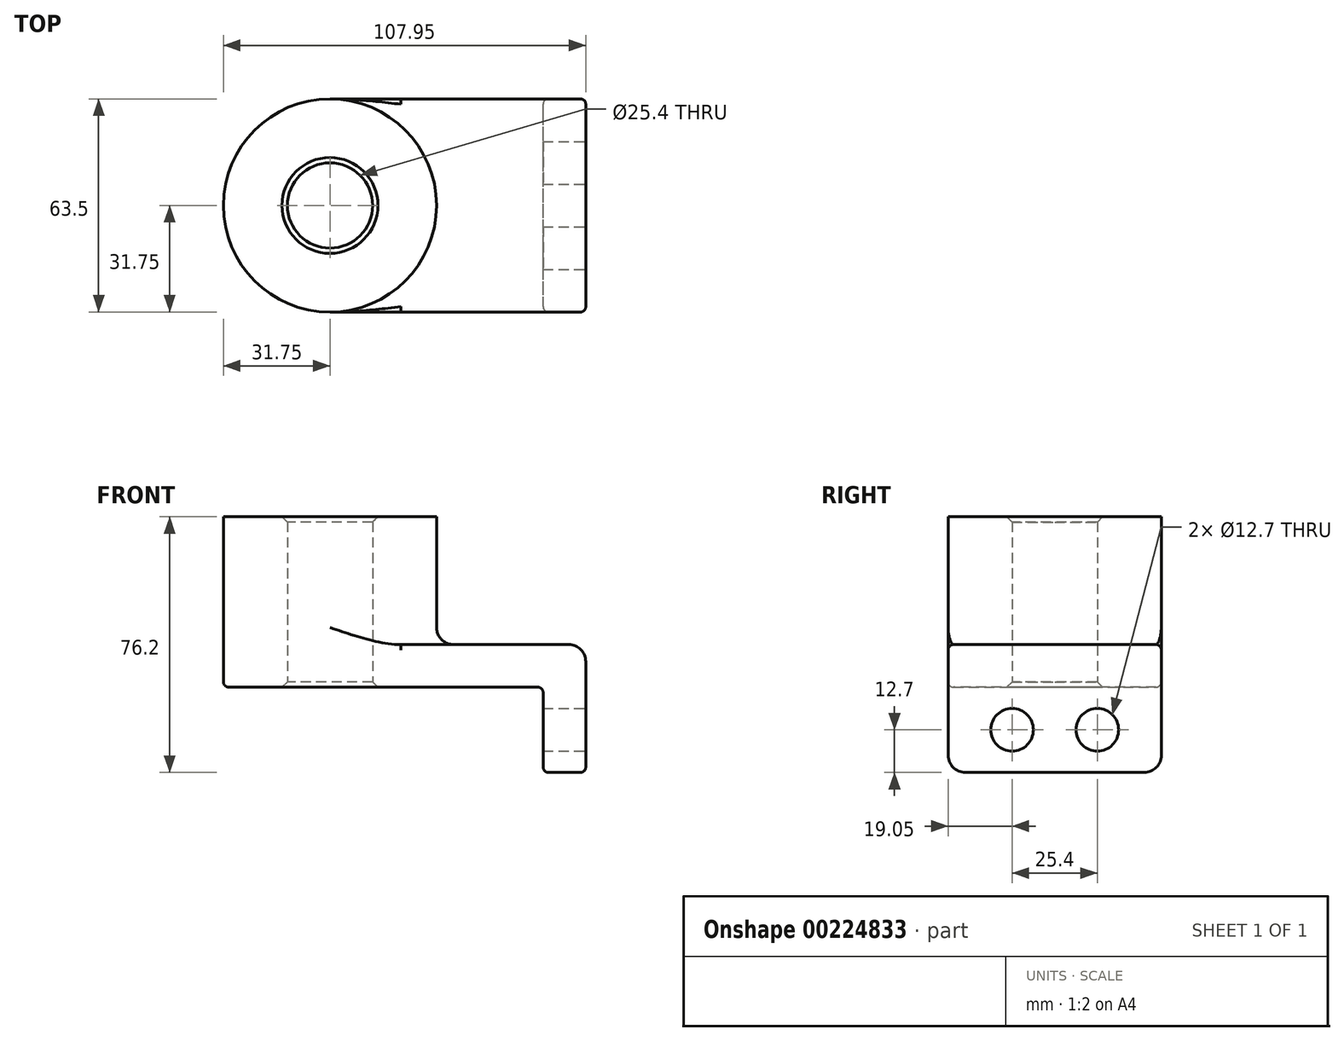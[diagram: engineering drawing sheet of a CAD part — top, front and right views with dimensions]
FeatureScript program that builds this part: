
annotation { "Feature Type Name" : "Feature", "Feature Type Description" : "" }
export const myFeature = defineFeature(function(context is Context, id is Id, definition is map)
    precondition{}
    {
        {
            var Q0;
            Q0=qCreatedBy(makeId("Top.planeOp"),FACE);
            var sketch = newSketch(context, id + "F0", { "sketchPlane" : qUnion([Q0])});
            skLineSegment(sketch, "E0.bottom", {"start": v(-38.1, 31.75) * mm, "end": v(38.1, 31.75) * mm});
            skLineSegment(sketch, "E0.top", {"start": v(-38.1, -31.75) * mm, "end": v(38.1, -31.75) * mm});
            skLineSegment(sketch, "E0.left", {"start": v(-38.1, 31.75) * mm, "end": v(-38.1, -31.75) * mm});
            skLineSegment(sketch, "E0.right", {"start": v(38.1, 31.75) * mm, "end": v(38.1, -31.75) * mm});
            skPoint(sketch, "E0.middle", {"position": v(0, 0) * mm});
            skCircle(sketch, "E1", {"center": v(-38.1, 0) * mm, "radius": 31.75 * mm});
            skCircle(sketch, "E2", {"center": v(-38.1, 0) * mm, "radius": 12.7 * mm});
            skSolve(sketch);
        }
        {
            var Q0;
            Q0 = qSketchRegion(id + "F0", true);
            extrude(context, id + "F1", {"entities" : qUnion([Q0]), "depth" : 12.7 * mm});
        }
        {
            var Q0;
            {var subQ1=sQuery(id+"F0.wireOp",EDGE,"E0.left");var subQ3=sQuery(id+"F0.wireOp",EDGE,"E2");var subQ4=makeQuery(id+"F0.imprint","INTERSECT",VERTEX,{"disambiguationData":[OD(0.0)],"derivedFrom":[subQ1,subQ3]});Q0=makeQuery(id+"F0.imprint","IMPRINT",FACE,{"disambiguationData":[TD([[makeQuery(id+"F0.imprint","IMPRINT",EDGE,{"disambiguationData":[TD([[subQ4,-1.0]])],"derivedFrom":subQ3}),-1.0]])]});}
            var Q1;
            {var subQ1=sQuery(id+"F0.wireOp",EDGE,"E0.left");var subQ3=sQuery(id+"F0.wireOp",EDGE,"E2");var subQ4=makeQuery(id+"F0.imprint","INTERSECT",VERTEX,{"disambiguationData":[OD(0.0)],"derivedFrom":[subQ1,subQ3]});Q1=makeQuery(id+"F0.imprint","IMPRINT",FACE,{"disambiguationData":[TD([[makeQuery(id+"F0.imprint","IMPRINT",EDGE,{"disambiguationData":[TD([[subQ4,1.0]])],"derivedFrom":subQ3}),-1.0]])]});}
            extrude(context, id + "F2", {"entities" : qUnion([Q0, Q1]), "operationType" : NewBodyOperationType.ADD, "depth" : 50.8 * mm});
        }
        {
            var Q0;
            Q0=makeQuery(id+"F1.opExtrude","SWEPT_FACE",FACE,{"disambiguationData":[OSD([sQuery(id+"F0.wireOp",EDGE,"E0.right")])]});
            var sketch = newSketch(context, id + "F3", { "sketchPlane" : qUnion([Q0])});
            skLineSegment(sketch, "E3.bottom", {"start": v(-31.75, 12.7) * mm, "end": v(31.75, 12.7) * mm});
            skLineSegment(sketch, "E3.top", {"start": v(-31.75, -25.4) * mm, "end": v(31.75, -25.4) * mm});
            skLineSegment(sketch, "E3.left", {"start": v(-31.75, 12.7) * mm, "end": v(-31.75, -25.4) * mm});
            skLineSegment(sketch, "E3.right", {"start": v(31.75, 12.7) * mm, "end": v(31.75, -25.4) * mm});
            skCircle(sketch, "E4", {"center": v(-12.7, -12.7) * mm, "radius": 6.35 * mm});
            skLineSegment(sketch, "E5", {"start": v(0, 0) * mm, "end": v(0, -25.4) * mm});
            skCircle(sketch, "E6.MirrorC", {"center": v(12.7, -12.7) * mm, "radius": 6.35 * mm});
            skSolve(sketch);
        }
        {
            var Q0;
            Q0 = qSketchRegion(id + "F3", true);
            extrude(context, id + "F4", {"entities" : qUnion([Q0]), "operationType" : NewBodyOperationType.ADD, "oppositeDirection" : true, "depth" : 12.7 * mm});
        }
        {
            var Q0;
            {var subQ0=sQuery(id+"F0.wireOp",EDGE,"E1");Q0=makeQuery(id+"F2.boolean.opBoolean","INTERSECT",EDGE,{"derivedFrom":[makeQuery(id+"F1.opExtrude","CAP_FACE",FACE,{"disambiguationData":[OSD([sQuery(id+"F0.wireOp",EDGE,"E0.bottom"),sQuery(id+"F0.wireOp",EDGE,"E0.top"),sQuery(id+"F0.wireOp",EDGE,"E0.right"),subQ0,sQuery(id+"F0.wireOp",EDGE,"E2")])],"isStart":false}),makeQuery(id+"F2.opExtrude","SWEPT_FACE",FACE,{"disambiguationData":[OSD([subQ0])]})]});}
            var Q1;
            Q1=makeQuery(id+"F1.opExtrude","CAP_EDGE",EDGE,{"disambiguationData":[OSD([sQuery(id+"F0.wireOp",EDGE,"E0.right")])],"isStart":false});
            var Q2;
            Q2=makeQuery(id+"F4.opExtrude","SWEPT_EDGE",EDGE,{"disambiguationData":[OSD([sQuery(id+"F3.wireOp",EDGE,"E3.top"),sQuery(id+"F3.wireOp",EDGE,"E3.left")])]});
            var Q3;
            Q3=makeQuery(id+"F4.opExtrude","SWEPT_EDGE",EDGE,{"disambiguationData":[OSD([sQuery(id+"F3.wireOp",EDGE,"E3.top"),sQuery(id+"F3.wireOp",EDGE,"E3.right")])]});
            fillet(context, id + "F5", {"entities" : qUnion([Q0, Q1, Q2, Q3]), "radius" : 5.08 * mm, "tangentPropagation" : true, "allowEdgeOverflow" : false});
        }
        {
            var Q0;
            Q0=makeQuery(id+"F1.opExtrude","CAP_EDGE",EDGE,{"disambiguationData":[OSD([sQuery(id+"F0.wireOp",EDGE,"E0.top")])],"isStart":false});
            var Q1;
            Q1=makeQuery(id+"F4.boolean.opBoolean","INTERSECT",EDGE,{"derivedFrom":[makeQuery(id+"F1.opExtrude","CAP_FACE",FACE,{"disambiguationData":[OSD([sQuery(id+"F0.wireOp",EDGE,"E0.bottom"),sQuery(id+"F0.wireOp",EDGE,"E0.top"),sQuery(id+"F0.wireOp",EDGE,"E0.right"),sQuery(id+"F0.wireOp",EDGE,"E1"),sQuery(id+"F0.wireOp",EDGE,"E2")])],"isStart":true}),makeQuery(id+"F4.opExtrude","CAP_FACE",FACE,{"disambiguationData":[OSD([sQuery(id+"F3.wireOp",EDGE,"E3.bottom"),sQuery(id+"F3.wireOp",EDGE,"E3.top"),sQuery(id+"F3.wireOp",EDGE,"E3.left"),sQuery(id+"F3.wireOp",EDGE,"E3.right"),sQuery(id+"F3.wireOp",EDGE,"E4"),sQuery(id+"F3.wireOp",EDGE,"E6.MirrorC")])],"isStart":false})]});
            var Q2;
            Q2=makeQuery(id+"F1.opExtrude","CAP_EDGE",EDGE,{"disambiguationData":[OSD([sQuery(id+"F0.wireOp",EDGE,"E0.bottom")])],"isStart":false});
            fillet(context, id + "F6", {"entities" : qUnion([Q0, Q1, Q2]), "radius" : 1.59 * mm, "tangentPropagation" : true, "allowEdgeOverflow" : false});
        }
        {
            var Q0;
            Q0=makeQuery(id+"F1.opExtrude","CAP_EDGE",EDGE,{"disambiguationData":[OSD([sQuery(id+"F0.wireOp",EDGE,"E0.bottom")])],"isStart":true});
            var Q1;
            Q1=makeQuery(id+"F1.opExtrude","CAP_EDGE",EDGE,{"disambiguationData":[OSD([sQuery(id+"F0.wireOp",EDGE,"E0.top")])],"isStart":true});
            fillet(context, id + "F7", {"entities" : qUnion([Q0, Q1]), "radius" : 1.59 * mm, "tangentPropagation" : true, "allowEdgeOverflow" : false});
        }
        {
            var Q0;
            Q0=makeQuery(id+"F2.opExtrude","CAP_EDGE",EDGE,{"disambiguationData":[OSD([sQuery(id+"F0.wireOp",EDGE,"E2")])],"isStart":false});
            var Q1;
            {var subQ0=sQuery(id+"F0.wireOp",EDGE,"E2");Q1=makeQuery(id+"F2.boolean.opBoolean","MERGE",FACE,{"derivedFrom":[makeQuery(id+"F1.opExtrude","SWEPT_FACE",FACE,{"disambiguationData":[OSD([subQ0])]}),makeQuery(id+"F2.opExtrude","SWEPT_FACE",FACE,{"disambiguationData":[OSD([subQ0])]})]});}
            chamfer(context, id + "F8", {"entities" : qUnion([Q0, Q1]), "width" : 1.59 * mm, "tangentPropagation" : true});
        }
    });
